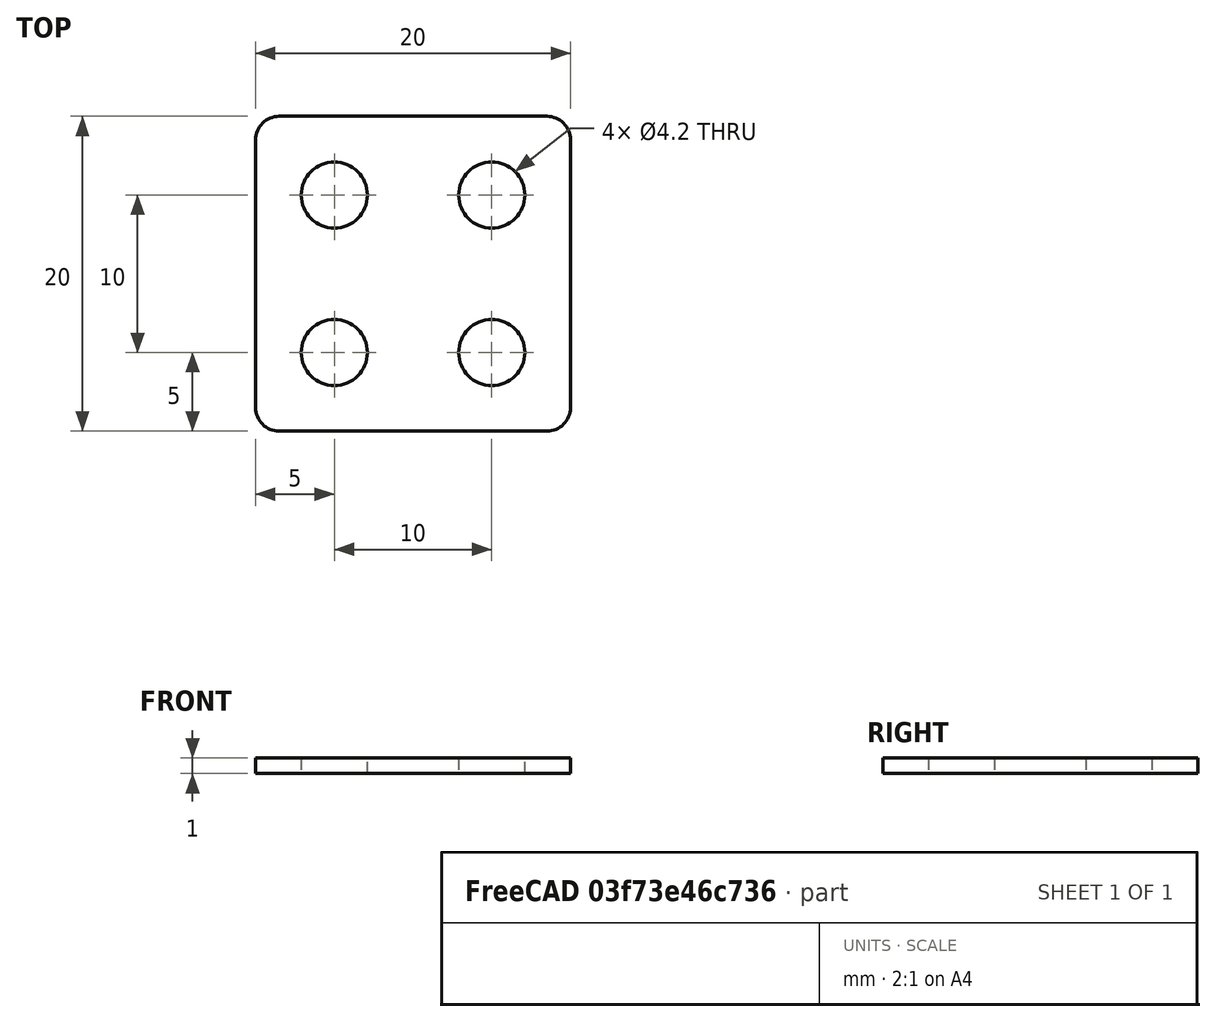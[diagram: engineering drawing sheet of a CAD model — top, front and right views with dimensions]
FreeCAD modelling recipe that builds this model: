
FCSTD DOCUMENT  (FreeCAD 0.16RUnknown)
Label: strip_2x2
License: All rights reserved
LicenseURL: http://en.wikipedia.org/wiki/All_rights_reserved
objects: Sketcher::SketchObject×1, PartDesign::Pad×1
note: 3 computed .brp shape members not serialized (recipe doc carries the construction recipe); baked Part::Feature solids carry a one-line shape summary decoded from their .brp

FEATURE [Sketcher::SketchObject] Sketch
  sketch-geometry (12):
    g0: Circle CenterX=-10 CenterY=10 CenterZ=0 NormalX=0 NormalY=0 NormalZ=1 Radius=2.1
    g1: Circle CenterX=0 CenterY=10 CenterZ=0 NormalX=0 NormalY=0 NormalZ=1 Radius=2.1
    g2: Circle CenterX=-10 CenterY=0 CenterZ=0 NormalX=0 NormalY=0 NormalZ=1 Radius=2.1
    g3: Circle CenterX=0 CenterY=0 CenterZ=0 NormalX=0 NormalY=0 NormalZ=1 Radius=2.1
    g4: LineSegment StartX=-13.5 StartY=15 StartZ=0 EndX=3.5 EndY=15 EndZ=0
    g5: LineSegment StartX=5 StartY=13.5 StartZ=0 EndX=5 EndY=-3.5 EndZ=0
    g6: LineSegment StartX=3.5 StartY=-5 StartZ=0 EndX=-13.5 EndY=-5 EndZ=0
    g7: LineSegment StartX=-15 StartY=-3.5 StartZ=0 EndX=-15 EndY=13.5 EndZ=0
    g8: ArcOfCircle CenterX=3.5 CenterY=13.5 CenterZ=0 NormalX=0 NormalY=0 NormalZ=1 Radius=1.5 StartAngle=0 EndAngle=1.5708
    g9: ArcOfCircle CenterX=3.5 CenterY=-3.5 CenterZ=0 NormalX=0 NormalY=0 NormalZ=1 Radius=1.5 StartAngle=4.71239 EndAngle=6.28319
    g10: ArcOfCircle CenterX=-13.5 CenterY=-3.5 CenterZ=0 NormalX=0 NormalY=0 NormalZ=1 Radius=1.5 StartAngle=3.14159 EndAngle=4.71239
    g11: ArcOfCircle CenterX=-13.5 CenterY=13.5 CenterZ=0 NormalX=0 NormalY=0 NormalZ=1 Radius=1.5 StartAngle=1.5708 EndAngle=3.14159
  constraints (31):
    c: Equal(g0,g2) = 2.1
    c: Coincident(g3,g-1)
    c: Distance(g-1,g2) = 10
    c: Distance(g-1,g1) = 10
    c: PointOnObject(g2,g-1)
    c: PointOnObject(g1,g-2)
    c: Distance(g0,g2) = 10
    c: Distance(g0,g1) = 10
    c: Horizontal(g4)
    c: Horizontal(g6)
    c: Vertical(g5)
    c: Vertical(g7)
    c: Tangent(g4,g8) = 1.5708
    c: Tangent(g5,g8) = 1.5708
    c: Tangent(g5,g9) = 1.5708
    c: Tangent(g6,g9) = 1.5708
    c: Tangent(g7,g10) = 1.5708
    c: Tangent(g6,g10) = 1.5708
    c: Tangent(g7,g11) = 1.5708
    c: Tangent(g4,g11) = 1.5708
    c: Equal(g0,g1)
    c: Equal(g2,g3)
    c: Radius(g0) = 2.1
    c: DistanceX(g7,g5) = 20
    c: DistanceY(g6,g4) = 20
    c: Equal(g11,g8)
    c: Equal(g8,g10)
    c: Equal(g10,g9)
    c: Radius(g11) = 1.5
    c: DistanceX(g7,g2) = 5
    c: DistanceY(g6,g2) = 5
FEATURE [PartDesign::Pad] Pad
  Length = 1
  Length2 = 100
  Sketch = -> Sketch
  Type = 0
